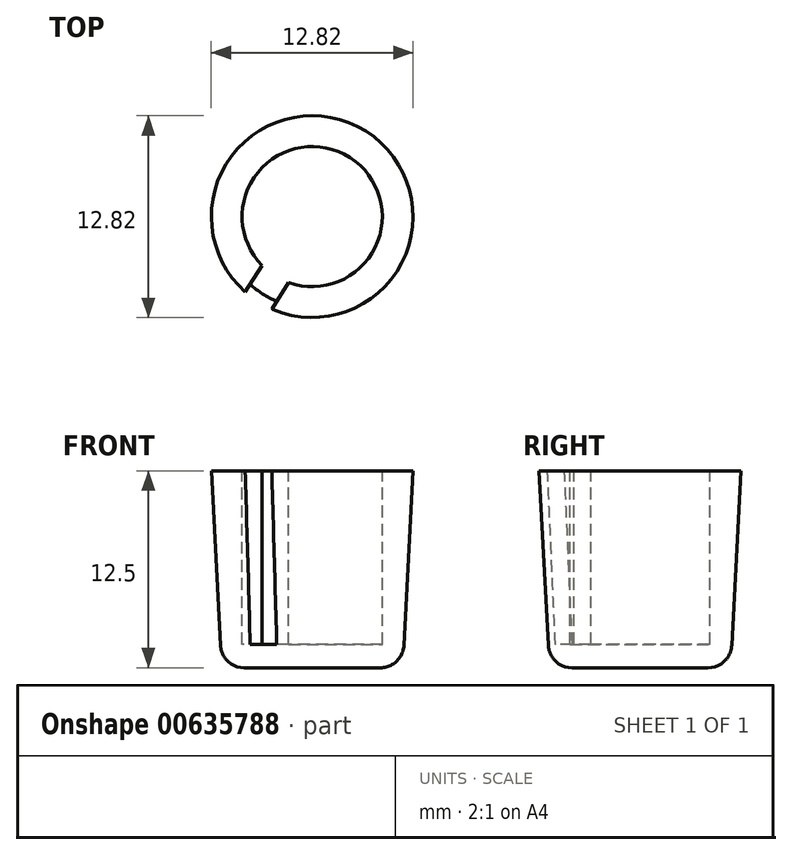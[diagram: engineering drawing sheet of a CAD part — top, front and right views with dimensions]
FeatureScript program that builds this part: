
annotation { "Feature Type Name" : "Feature", "Feature Type Description" : "" }
export const myFeature = defineFeature(function(context is Context, id is Id, definition is map)
    precondition{}
    {
        {
            var Q0;
            Q0=qCreatedBy(makeId("Top.planeOp"),FACE);
            var sketch = newSketch(context, id + "F0", { "sketchPlane" : qUnion([Q0])});
            skCircle(sketch, "E0.0", {"center": v(0, 0) * mm, "radius": 5.75 * mm});
            skSolve(sketch);
        }
        {
            var Q0;
            Q0 = qSketchRegion(id + "F0", true);
            extrude(context, id + "F1", {"entities" : qUnion([Q0]), "depth" : 12.5 * mm, "offsetDistance" : 25 * mm, "hasDraft" : true, "draftAngle" : 3 * degree});
        }
        {
            var Q0;
            Q0=makeQuery(id+"F1.opExtrude","CAP_FACE",FACE,{"disambiguationData":[OSD([sQuery(id+"F0.wireOp",EDGE,"E0.0")])],"isStart":false});
            var sketch = newSketch(context, id + "F2", { "sketchPlane" : qUnion([Q0])});
            skArc(sketch, "E1", {"start": v(-1.5, -4.2) * mm, "mid": v(2.4, 3.75) * mm, "end": v(-3.18, -3.11) * mm});
            skLineSegment(sketch, "E2.0", {"start": v(-3.18, -3.11) * mm, "end": v(-6.52, -8.33) * mm});
            skLineSegment(sketch, "E3.0", {"start": v(-1.5, -4.2) * mm, "end": v(-4.83, -9.4) * mm});
            skLineSegment(sketch, "E4", {"start": v(-6.52, -8.33) * mm, "end": v(-4.83, -9.4) * mm});
            skSolve(sketch);
        }
        {
            var Q0;
            Q0 = qSketchRegion(id + "F2", true);
            extrude(context, id + "F3", {"entities" : qUnion([Q0]), "operationType" : NewBodyOperationType.REMOVE, "oppositeDirection" : true, "depth" : 11 * mm, "offsetDistance" : 25 * mm});
        }
        {
            var Q0;
            Q0=makeQuery(id+"F1.opExtrude","CAP_EDGE",EDGE,{"disambiguationData":[OSD([sQuery(id+"F0.wireOp",EDGE,"E0.0")])],"isStart":true});
            fillet(context, id + "F4", {"entities" : qUnion([Q0]), "radius" : 1.5 * mm, "tangentPropagation" : true, "allowEdgeOverflow" : false});
        }
    });
